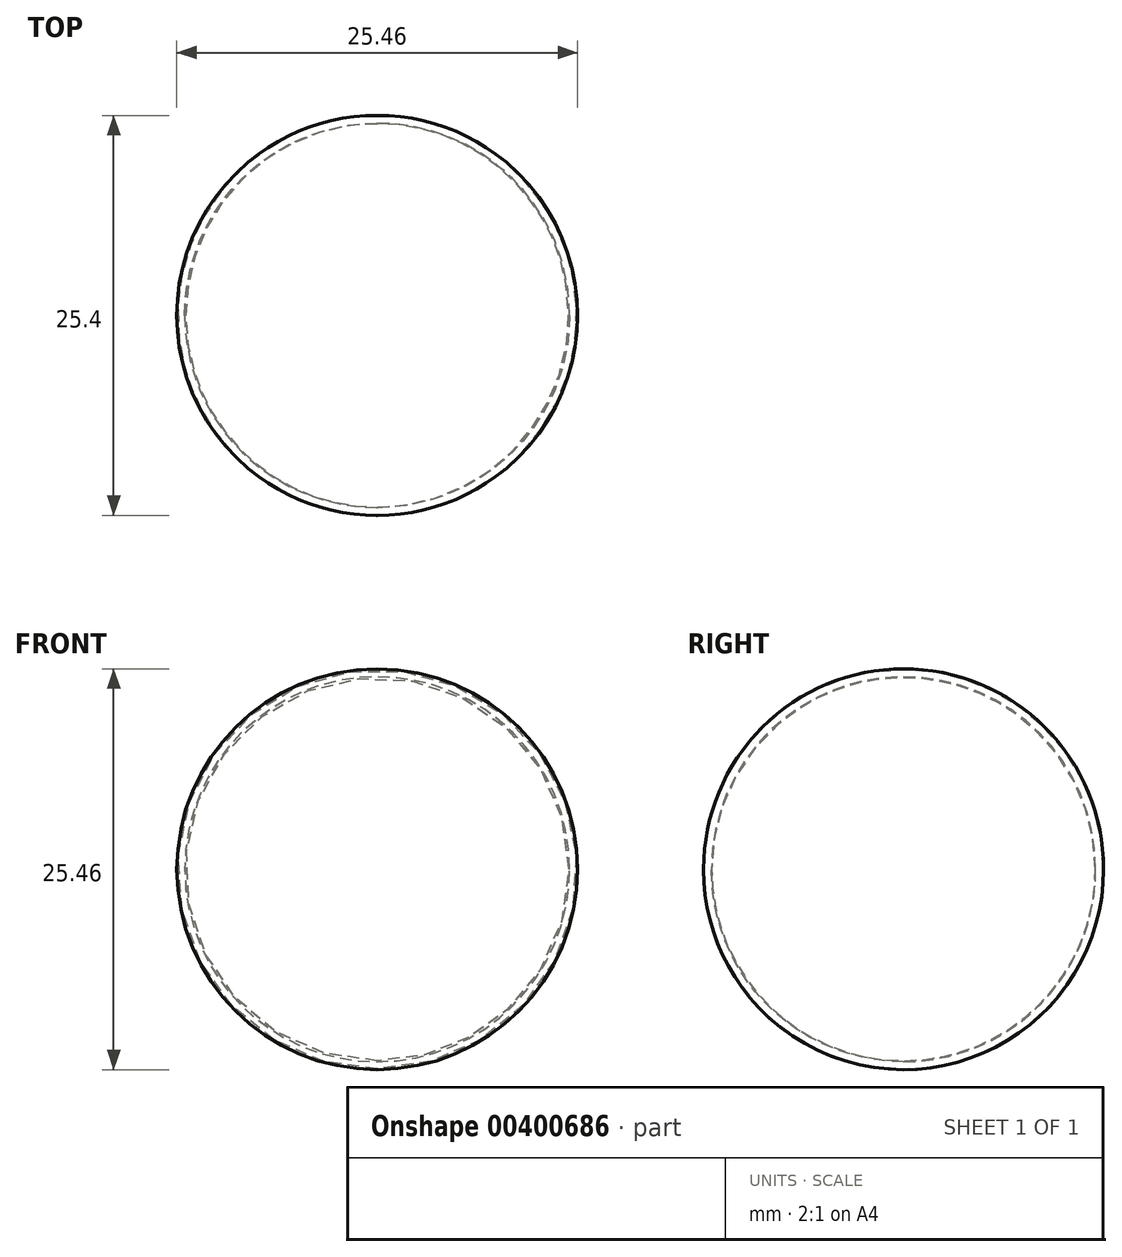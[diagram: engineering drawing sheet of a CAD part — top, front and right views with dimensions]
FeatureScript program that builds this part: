
annotation { "Feature Type Name" : "Feature", "Feature Type Description" : "" }
export const myFeature = defineFeature(function(context is Context, id is Id, definition is map)
    precondition{}
    {
        {
            var Q0;
            Q0=qCreatedBy(makeId("Top.planeOp"),FACE);
            var sketch = newSketch(context, id + "F0", { "sketchPlane" : qUnion([Q0])});
            skLineSegment(sketch, "E0", {"start": v(-56.77, 31.3) * mm, "end": v(-56.77, 5.9) * mm});
            skArc(sketch, "E1", {"start": v(-56.77, 5.9) * mm, "mid": v(-44.1, 18.6) * mm, "end": v(-56.77, 31.3) * mm});
            skSolve(sketch);
        }
        {
            var Q0;
            Q0 = qSketchRegion(id + "F0", true);
            var Q1;
            Q1=sQuery(id+"F0.wireOp",EDGE,"E0");
            revolve(context, id + "F1", {"entities" : qUnion([Q0]), "axis" : qUnion([Q1]), "revolveType" : RevolveType.FULL});
        }
        {
            var Q0;
            Q0=makeQuery(id+"F1.opRevolve","SWEPT_FACE",FACE,{"disambiguationData":[OSD([sQuery(id+"F0.wireOp",EDGE,"E1")])]});
            var Q1;
            Q1=makeQuery(id+"F1.opRevolve","SWEPT_BODY",BODY,{"disambiguationData":[OSD([sQuery(id+"F0.wireOp",EDGE,"E0"),sQuery(id+"F0.wireOp",EDGE,"E1")])]});
            shell(context, id + "F2", {"isHollow" : true, "entities" : qUnion([Q0]), "parts" : qUnion([Q1]), "thickness" : 0.5 * mm});
        }
    });
